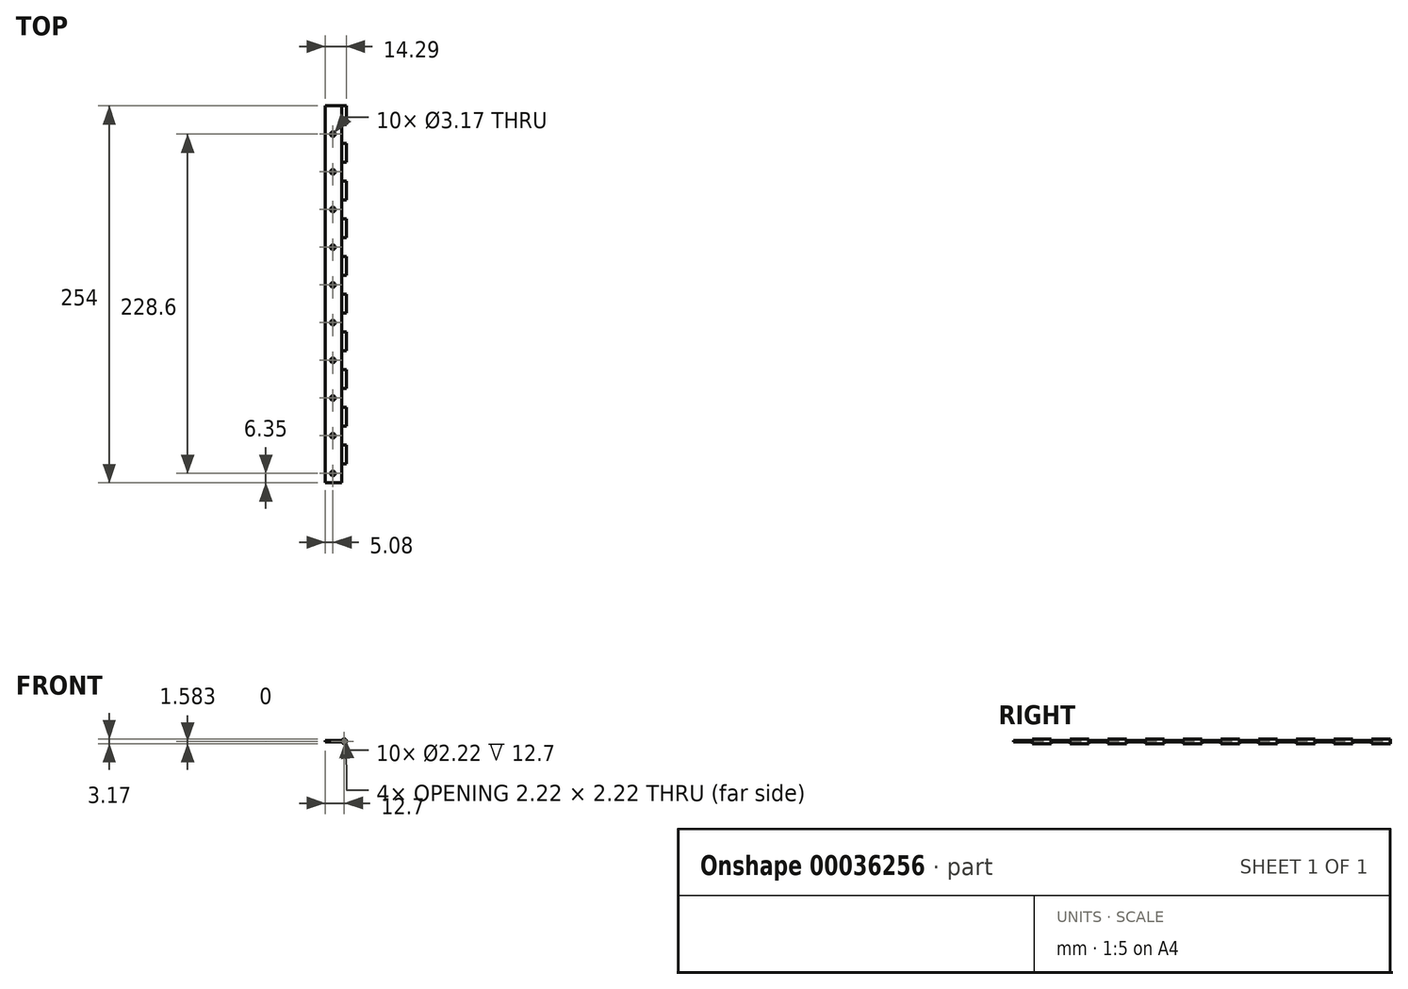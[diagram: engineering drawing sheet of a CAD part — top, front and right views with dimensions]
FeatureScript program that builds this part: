
annotation { "Feature Type Name" : "Feature", "Feature Type Description" : "" }
export const myFeature = defineFeature(function(context is Context, id is Id, definition is map)
    precondition{}
    {
        {
            var Q0;
            Q0=qCreatedBy(makeId("Front.planeOp"),FACE);
            var sketch = newSketch(context, id + "F0", { "sketchPlane" : qUnion([Q0])});
            skLineSegment(sketch, "E0.bottom", {"start": v(0, 0) * mm, "end": v(11.2, 0) * mm});
            skLineSegment(sketch, "E0.top", {"start": v(0, 1.07) * mm, "end": v(11.2, 1.07) * mm});
            skLineSegment(sketch, "E0.left", {"start": v(0, 0) * mm, "end": v(0, 1.07) * mm});
            skArc(sketch, "E1", {"start": v(11.2, 0) * mm, "mid": v(14.29, 0.53) * mm, "end": v(11.2, 1.07) * mm});
            skCircle(sketch, "E2", {"center": v(12.7, 0.53) * mm, "radius": 1.11 * mm});
            skSolve(sketch);
        }
        {
            var Q0;
            Q0=qSketchRegion(id+"F0",true);
            extrude(context, id + "F1", {"entities" : qUnion([Q0]), "depth" : 254 * mm});
        }
        {
            var Q0;
            Q0=makeQuery(id+"F1.opExtrude","SWEPT_FACE",FACE,{"disambiguationData":[OSD([sQuery(id+"F0.wireOp",EDGE,"E0.top")])]});
            var sketch = newSketch(context, id + "F2", { "sketchPlane" : qUnion([Q0])});
            skLineSegment(sketch, "E3", {"start": v(10.95, -241.3) * mm, "end": v(14.7, -241.3) * mm});
            skLineSegment(sketch, "E4", {"start": v(14.7, -241.3) * mm, "end": v(14.7, -254) * mm});
            skLineSegment(sketch, "E5", {"start": v(14.7, -254) * mm, "end": v(10.95, -254) * mm});
            skLineSegment(sketch, "E6.0", {"start": v(10.95, -254) * mm, "end": v(10.95, -241.3) * mm});
            skPoint(sketch, "E7.orphan", {"position": v(11.2, -254) * mm});
            skLineSegment(sketch, "E8.0.1.0", {"start": v(14.7, -215.9) * mm, "end": v(14.7, -228.6) * mm});
            skLineSegment(sketch, "E8.0.1.1", {"start": v(10.95, -215.9) * mm, "end": v(14.7, -215.9) * mm});
            skLineSegment(sketch, "E8.0.1.2", {"start": v(10.95, -228.6) * mm, "end": v(10.95, -215.9) * mm});
            skLineSegment(sketch, "E8.0.1.3", {"start": v(14.7, -228.6) * mm, "end": v(10.95, -228.6) * mm});
            skLineSegment(sketch, "E8.0.2.0", {"start": v(14.7, -190.5) * mm, "end": v(14.7, -203.2) * mm});
            skLineSegment(sketch, "E8.0.2.1", {"start": v(10.95, -190.5) * mm, "end": v(14.7, -190.5) * mm});
            skLineSegment(sketch, "E8.0.2.2", {"start": v(10.95, -203.2) * mm, "end": v(10.95, -190.5) * mm});
            skLineSegment(sketch, "E8.0.2.3", {"start": v(14.7, -203.2) * mm, "end": v(10.95, -203.2) * mm});
            skLineSegment(sketch, "E8.0.3.0", {"start": v(14.7, -165.1) * mm, "end": v(14.7, -177.8) * mm});
            skLineSegment(sketch, "E8.0.3.1", {"start": v(10.95, -165.1) * mm, "end": v(14.7, -165.1) * mm});
            skLineSegment(sketch, "E8.0.3.2", {"start": v(10.95, -177.8) * mm, "end": v(10.95, -165.1) * mm});
            skLineSegment(sketch, "E8.0.3.3", {"start": v(14.7, -177.8) * mm, "end": v(10.95, -177.8) * mm});
            skLineSegment(sketch, "E8.0.4.0", {"start": v(14.7, -139.7) * mm, "end": v(14.7, -152.4) * mm});
            skLineSegment(sketch, "E8.0.4.1", {"start": v(10.95, -139.7) * mm, "end": v(14.7, -139.7) * mm});
            skLineSegment(sketch, "E8.0.4.2", {"start": v(10.95, -152.4) * mm, "end": v(10.95, -139.7) * mm});
            skLineSegment(sketch, "E8.0.4.3", {"start": v(14.7, -152.4) * mm, "end": v(10.95, -152.4) * mm});
            skLineSegment(sketch, "E8.0.5.0", {"start": v(14.7, -114.3) * mm, "end": v(14.7, -127) * mm});
            skLineSegment(sketch, "E8.0.5.1", {"start": v(10.95, -114.3) * mm, "end": v(14.7, -114.3) * mm});
            skLineSegment(sketch, "E8.0.5.2", {"start": v(10.95, -127) * mm, "end": v(10.95, -114.3) * mm});
            skLineSegment(sketch, "E8.0.5.3", {"start": v(14.7, -127) * mm, "end": v(10.95, -127) * mm});
            skLineSegment(sketch, "E8.0.6.0", {"start": v(14.7, -88.9) * mm, "end": v(14.7, -101.6) * mm});
            skLineSegment(sketch, "E8.0.6.1", {"start": v(10.95, -88.9) * mm, "end": v(14.7, -88.9) * mm});
            skLineSegment(sketch, "E8.0.6.2", {"start": v(10.95, -101.6) * mm, "end": v(10.95, -88.9) * mm});
            skLineSegment(sketch, "E8.0.6.3", {"start": v(14.7, -101.6) * mm, "end": v(10.95, -101.6) * mm});
            skLineSegment(sketch, "E8.0.7.0", {"start": v(14.7, -63.5) * mm, "end": v(14.7, -76.2) * mm});
            skLineSegment(sketch, "E8.0.7.1", {"start": v(10.95, -63.5) * mm, "end": v(14.7, -63.5) * mm});
            skLineSegment(sketch, "E8.0.7.2", {"start": v(10.95, -76.2) * mm, "end": v(10.95, -63.5) * mm});
            skLineSegment(sketch, "E8.0.7.3", {"start": v(14.7, -76.2) * mm, "end": v(10.95, -76.2) * mm});
            skLineSegment(sketch, "E8.0.8.0", {"start": v(14.7, -38.1) * mm, "end": v(14.7, -50.8) * mm});
            skLineSegment(sketch, "E8.0.8.1", {"start": v(10.95, -38.1) * mm, "end": v(14.7, -38.1) * mm});
            skLineSegment(sketch, "E8.0.8.2", {"start": v(10.95, -50.8) * mm, "end": v(10.95, -38.1) * mm});
            skLineSegment(sketch, "E8.0.8.3", {"start": v(14.7, -50.8) * mm, "end": v(10.95, -50.8) * mm});
            skLineSegment(sketch, "E8.0.9.0", {"start": v(14.7, -12.7) * mm, "end": v(14.7, -25.4) * mm});
            skLineSegment(sketch, "E8.0.9.1", {"start": v(10.95, -12.7) * mm, "end": v(14.7, -12.7) * mm});
            skLineSegment(sketch, "E8.0.9.2", {"start": v(10.95, -25.4) * mm, "end": v(10.95, -12.7) * mm});
            skLineSegment(sketch, "E8.0.9.3", {"start": v(14.7, -25.4) * mm, "end": v(10.95, -25.4) * mm});
            skLineSegment(sketch, "E8.direction1", {"start": v(14.7, -254) * mm, "end": v(40.1, -254) * mm, "construction": true});
            skLineSegment(sketch, "E8.direction2", {"start": v(14.7, -254) * mm, "end": v(14.7, -228.6) * mm, "construction": true});
            skSolve(sketch);
        }
        {
            var Q0;
            Q0=qSketchRegion(id+"F2",true);
            extrude(context, id + "F3", {"entities" : qUnion([Q0]), "operationType" : NewBodyOperationType.REMOVE, "endBound" : BoundingType.SYMMETRIC, "oppositeDirection" : true, "depth" : 25.4 * mm});
        }
        {
            var Q0;
            Q0=makeQuery(id+"F1.opExtrude","SWEPT_FACE",FACE,{"disambiguationData":[OSD([sQuery(id+"F0.wireOp",EDGE,"E0.top")])]});
            var sketch = newSketch(context, id + "F4", { "sketchPlane" : qUnion([Q0])});
            skCircle(sketch, "E9", {"center": v(5.08, -247.65) * mm, "radius": 1.59 * mm});
            skCircle(sketch, "E10.0.1.0", {"center": v(5.08, -222.25) * mm, "radius": 1.59 * mm});
            skCircle(sketch, "E10.0.2.0", {"center": v(5.08, -196.85) * mm, "radius": 1.59 * mm});
            skCircle(sketch, "E10.0.3.0", {"center": v(5.08, -171.45) * mm, "radius": 1.59 * mm});
            skCircle(sketch, "E10.0.4.0", {"center": v(5.08, -146.05) * mm, "radius": 1.59 * mm});
            skCircle(sketch, "E10.0.5.0", {"center": v(5.08, -120.65) * mm, "radius": 1.59 * mm});
            skCircle(sketch, "E10.0.6.0", {"center": v(5.08, -95.25) * mm, "radius": 1.59 * mm});
            skCircle(sketch, "E10.0.7.0", {"center": v(5.08, -69.85) * mm, "radius": 1.59 * mm});
            skCircle(sketch, "E10.0.8.0", {"center": v(5.08, -44.45) * mm, "radius": 1.59 * mm});
            skCircle(sketch, "E10.0.9.0", {"center": v(5.08, -19.05) * mm, "radius": 1.59 * mm});
            skLineSegment(sketch, "E10.direction1", {"start": v(5.08, -247.65) * mm, "end": v(30.48, -247.65) * mm, "construction": true});
            skLineSegment(sketch, "E10.direction2", {"start": v(5.08, -247.65) * mm, "end": v(5.08, -222.25) * mm, "construction": true});
            skSolve(sketch);
        }
        {
            var Q0;
            Q0=qSketchRegion(id+"F4",true);
            extrude(context, id + "F5", {"entities" : qUnion([Q0]), "operationType" : NewBodyOperationType.REMOVE, "oppositeDirection" : true, "depth" : 25.4 * mm});
        }
    });
